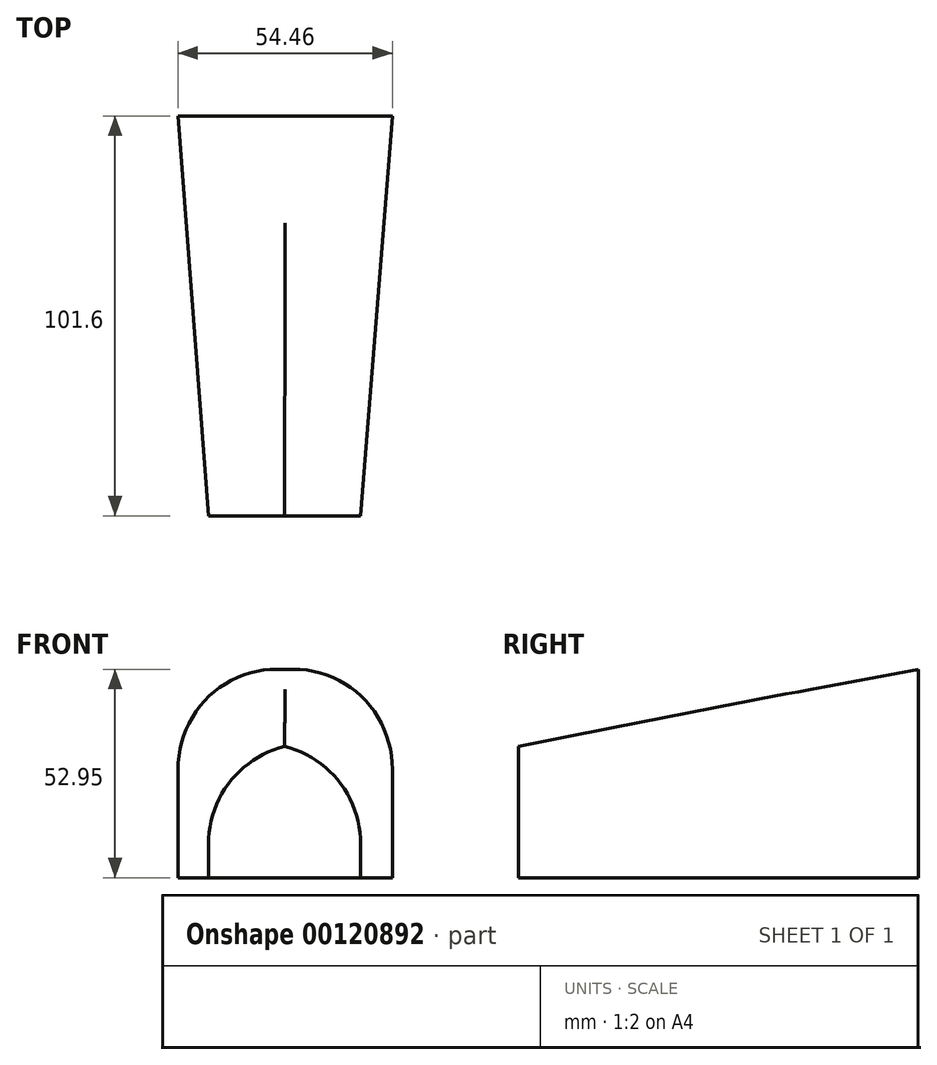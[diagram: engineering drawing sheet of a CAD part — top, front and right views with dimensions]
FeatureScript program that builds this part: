
annotation { "Feature Type Name" : "Feature", "Feature Type Description" : "" }
export const myFeature = defineFeature(function(context is Context, id is Id, definition is map)
    precondition{}
    {
        {
            var Q0;
            Q0=qCreatedBy(makeId("Front.planeOp"),FACE);
            var sketch = newSketch(context, id + "F0", { "sketchPlane" : qUnion([Q0])});
            skLineSegment(sketch, "E0.bottom", {"start": v(-27.72, 52.95) * mm, "end": v(26.74, 52.95) * mm});
            skLineSegment(sketch, "E0.top", {"start": v(-27.72, 0) * mm, "end": v(26.74, 0) * mm});
            skLineSegment(sketch, "E0.left", {"start": v(-27.72, 52.95) * mm, "end": v(-27.72, 0) * mm});
            skLineSegment(sketch, "E0.right", {"start": v(26.74, 52.95) * mm, "end": v(26.74, 0) * mm});
            skSolve(sketch);
        }
        {
            var Q0;
            Q0=qCreatedBy(makeId("Front.planeOp"),FACE);
            cPlane(context, id + "F1", {"entities" : qUnion([Q0]), "cplaneType" : CPlaneType.OFFSET, "offset" : 101.6 * mm, "width" : 152.4 * mm, "height" : 152.4 * mm});
        }
        {
            var Q0;
            Q0=qCreatedBy(id+"F1.planeOp",FACE);
            var sketch = newSketch(context, id + "F2", { "sketchPlane" : qUnion([Q0])});
            skLineSegment(sketch, "E1.bottom", {"start": v(-19.97, 0) * mm, "end": v(18.7, 0) * mm});
            skLineSegment(sketch, "E1.top", {"start": v(-19.97, 33.96) * mm, "end": v(18.7, 33.96) * mm});
            skLineSegment(sketch, "E1.left", {"start": v(-19.97, 0) * mm, "end": v(-19.97, 33.96) * mm});
            skLineSegment(sketch, "E1.right", {"start": v(18.7, 0) * mm, "end": v(18.7, 33.96) * mm});
            skSolve(sketch);
        }
        {
            var Q0;
            Q0=makeQuery(id+"F0.imprint","IMPRINT",FACE,{"disambiguationData":[TD([[makeQuery(id+"F0.imprint","IMPRINT",EDGE,{"derivedFrom":sQuery(id+"F0.wireOp",EDGE,"E0.bottom")}),-1.0]])]});
            var Q1;
            Q1=makeQuery(id+"F2.imprint","IMPRINT",FACE,{"disambiguationData":[TD([[makeQuery(id+"F2.imprint","IMPRINT",EDGE,{"derivedFrom":sQuery(id+"F2.wireOp",EDGE,"E1.bottom")}),1.0]])]});
            loft(context, id + "F3", {"sheetProfilesArray" : [{ "sheetProfileEntities" : qUnion([Q0]) }, { "sheetProfileEntities" : qUnion([Q1]) }]});
        }
        {
            var Q0;
            Q0=makeQuery(id+"F3.opLoft","SWEPT_EDGE",EDGE,{"disambiguationData":[OSD([sQuery(id+"F0.wireOp",EDGE,"E0.bottom"),sQuery(id+"F0.wireOp",EDGE,"E0.left"),sQuery(id+"F2.wireOp",EDGE,"E1.top"),sQuery(id+"F2.wireOp",EDGE,"E1.left")])]});
            var Q1;
            Q1=makeQuery(id+"F3.opLoft","SWEPT_EDGE",EDGE,{"disambiguationData":[OSD([sQuery(id+"F0.wireOp",EDGE,"E0.bottom"),sQuery(id+"F0.wireOp",EDGE,"E0.right"),sQuery(id+"F2.wireOp",EDGE,"E1.top"),sQuery(id+"F2.wireOp",EDGE,"E1.right")])]});
            fillet(context, id + "F4", {"entities" : qUnion([Q0, Q1]), "radius" : 25.4 * mm, "tangentPropagation" : true, "allowEdgeOverflow" : false});
        }
    });
